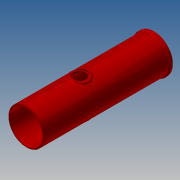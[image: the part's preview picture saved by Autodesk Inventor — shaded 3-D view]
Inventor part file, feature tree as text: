
AUTODESK INVENTOR PART (.ipt)
format: ipt  version: 2017.3 (Build 213257000, 257)  size: 337,408 bytes
history: native  units: in
note: dims shown in document units (in); Inventor stores cm internally (conversion verified against a paired STEP export)
features: extrude x10, sketch x8, fillet x3, chamfer x2, plane x2, pattern_circular x1, other x1, projected_geometry x1
ambient origin geometry x8: Origin, YZ Plane, XZ Plane, XY Plane, X Axis, Y Axis, Z Axis, Center Point
bodies: Solid1 (feature_tree)
feature tree (28):
  extrude  "Extrusion1"  Depth=31.0in
  extrude  "Extrusion2"  Depth=32.75in
  extrude  "Extrusion3"  Depth=32.48in
  chamfer  "Chamfer1"  Distance=1.0in
  extrude  "Extrusion4"  Depth=0.125in TaperAngle=45.0deg
  chamfer  "Chamfer2"  Distance=0.5in
  fillet  "Fillet1"  Radius=0.0312in
  extrude  "Extrusion5"  Depth=17.3228in
  plane  "Work Plane3"
  sketch  "Sketch7"  dims[d16=0.0312in d17=0.125in d18=45.0deg d19=0.0312in]
  extrude  "Extrusion9"  Depth=0.0312in
  extrude  "Extrusion11"  Depth=0.0312in TaperAngle=0.0deg
  sketch  "Sketch9"  dims[d22=11.1417in d23=46.9685in d24=0.5in d25=0.0in d39=15.1417in d40=1.0in d41=0.0in d42=12.75in d43=32.75in d44=110.0in d45=0.0in d48=2.0in d50=0.7874in d51=360.0deg d53=3.0in d54=1.0in d55=0.0in d56=1.0in d57=0.0in d58=0.0312in d59=0.5in d60=0.0in]
  extrude  "Extrusion12"  Depth=0.0312in
  extrude  "Extrusion13"  Depth=0.0312in TaperAngle=0.0deg
  fillet  "Fillet3"  Radius=12.75in
  fillet  "Fillet5"  Radius=32.75in
  pattern_circular  "Circular Pattern2"  [2 undecoded]
  sketch  "Sketch1"  dims[d0=28.5in d1=31.0in]
  sketch  "Sketch2"  dims[d2=110.0in d3=0.0in d4=32.75in]
  sketch  "Sketch3"  dims[d5=2.0in d6=0.0in d7=32.48in d8=1.0in d9=0.0in]
  sketch  "Sketch4"  dims[d10=0.875in d11=0.125in d12=45.0deg]
  sketch  "Sketch5"  dims[d13=29.98in d14=0.5in d15=0.0in]
  plane  "Work Plane2"
  sketch  "Sketch8"  dims[d20=2.5984in d21=17.3228in]
  other  "Srf1"
  projected_geometry  "Projected Loop1"
  extrude  "ExtrusionSrf1"  TaperAngle=0.0deg  [1 undecoded]
note: 3 required parameter values undecoded (feature->parameter linkage not recoverable at this tier; creation-order binding heuristic only, values carry confidence <= 0.55)
